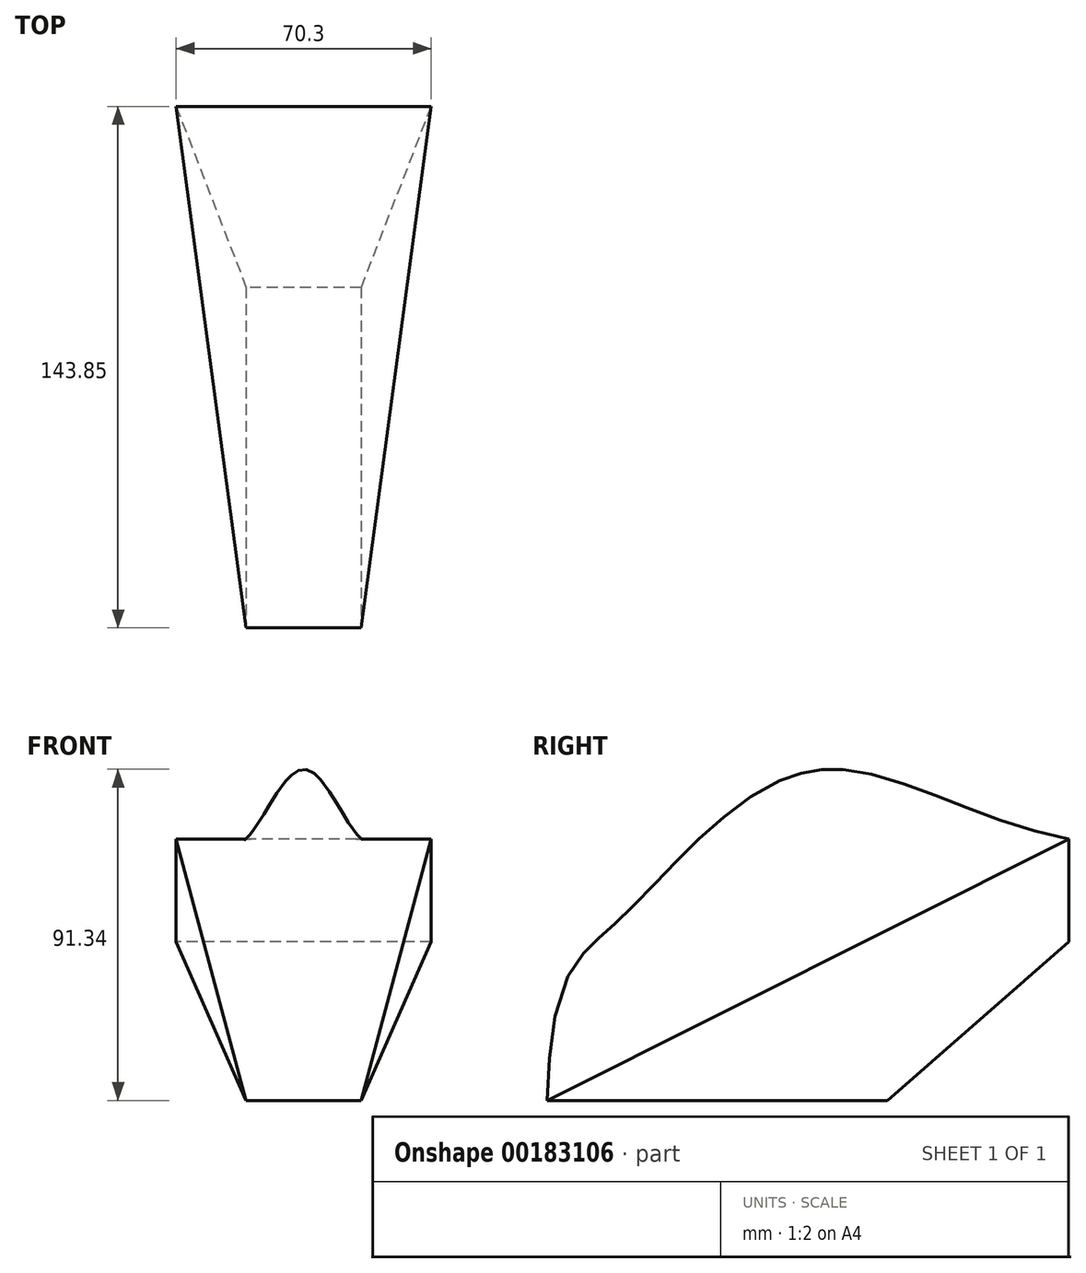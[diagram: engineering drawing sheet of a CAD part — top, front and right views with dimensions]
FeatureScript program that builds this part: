
annotation { "Feature Type Name" : "Feature", "Feature Type Description" : "" }
export const myFeature = defineFeature(function(context is Context, id is Id, definition is map)
    precondition{}
    {
        {
            var Q0;
            Q0=qCreatedBy(makeId("Front.planeOp"),FACE);
            var sketch = newSketch(context, id + "F0", { "sketchPlane" : qUnion([Q0])});
            skLineSegment(sketch, "E0.bottom", {"start": v(35.15, 72.11) * mm, "end": v(-35.15, 72.11) * mm});
            skLineSegment(sketch, "E0.top", {"start": v(35.15, 43.7) * mm, "end": v(-35.15, 43.7) * mm});
            skLineSegment(sketch, "E0.left", {"start": v(35.15, 72.11) * mm, "end": v(35.15, 43.7) * mm});
            skLineSegment(sketch, "E0.right", {"start": v(-35.15, 72.11) * mm, "end": v(-35.15, 43.7) * mm});
            skPoint(sketch, "E0.middle", {"position": v(0, 57.9) * mm});
            skSolve(sketch);
        }
        {
            var Q0;
            Q0=qCreatedBy(makeId("Top.planeOp"),FACE);
            var sketch = newSketch(context, id + "F1", { "sketchPlane" : qUnion([Q0])});
            skLineSegment(sketch, "E1.bottom", {"start": v(15.83, -49.93) * mm, "end": v(-15.83, -49.93) * mm});
            skLineSegment(sketch, "E1.top", {"start": v(15.83, -143.85) * mm, "end": v(-15.83, -143.85) * mm});
            skLineSegment(sketch, "E1.left", {"start": v(15.83, -49.93) * mm, "end": v(15.83, -143.85) * mm});
            skLineSegment(sketch, "E1.right", {"start": v(-15.83, -49.93) * mm, "end": v(-15.83, -143.85) * mm});
            skPoint(sketch, "E1.middle", {"position": v(0, -96.9) * mm});
            skSolve(sketch);
        }
        {
            var Q0;
            Q0=qCreatedBy(makeId("Right.planeOp"),FACE);
            var sketch = newSketch(context, id + "F2", { "sketchPlane" : qUnion([Q0])});
            skFitSpline(sketch, "E2", {"points": [v(0, 72.11) * mm, v(-72.3, 90.64) * mm, v(-123.17, 50.63) * mm, v(-143.85, 0) * mm], "startDerivative": vector(-235.83, 42.38) * mm, "endDerivative": vector(-8.6, -364.17) * mm});
            skSolve(sketch);
        }
        {
            var Q0;
            Q0=makeQuery(id+"F0.imprint","IMPRINT",FACE,{"disambiguationData":[TD([[makeQuery(id+"F0.imprint","IMPRINT",EDGE,{"derivedFrom":sQuery(id+"F0.wireOp",EDGE,"E0.bottom")}),1.0]])]});
            var Q1;
            Q1=makeQuery(id+"F1.imprint","IMPRINT",FACE,{"disambiguationData":[TD([[makeQuery(id+"F1.imprint","IMPRINT",EDGE,{"derivedFrom":sQuery(id+"F1.wireOp",EDGE,"E1.bottom")}),1.0]])]});
            var Q2;
            Q2=sQuery(id+"F2.wireOp",EDGE,"E2");
            loft(context, id + "F3", {"addGuides" : true, "sheetProfilesArray" : [{ "sheetProfileEntities" : qUnion([Q0]) }, { "sheetProfileEntities" : qUnion([Q1]) }], "guidesArray" : [{ "guideEntities" : qUnion([Q2]), "guideDerivativeType" : LoftGuideDerivativeType.DEFAULT, "guideDerivativeMagnitude" : 1 }]});
        }
    });
